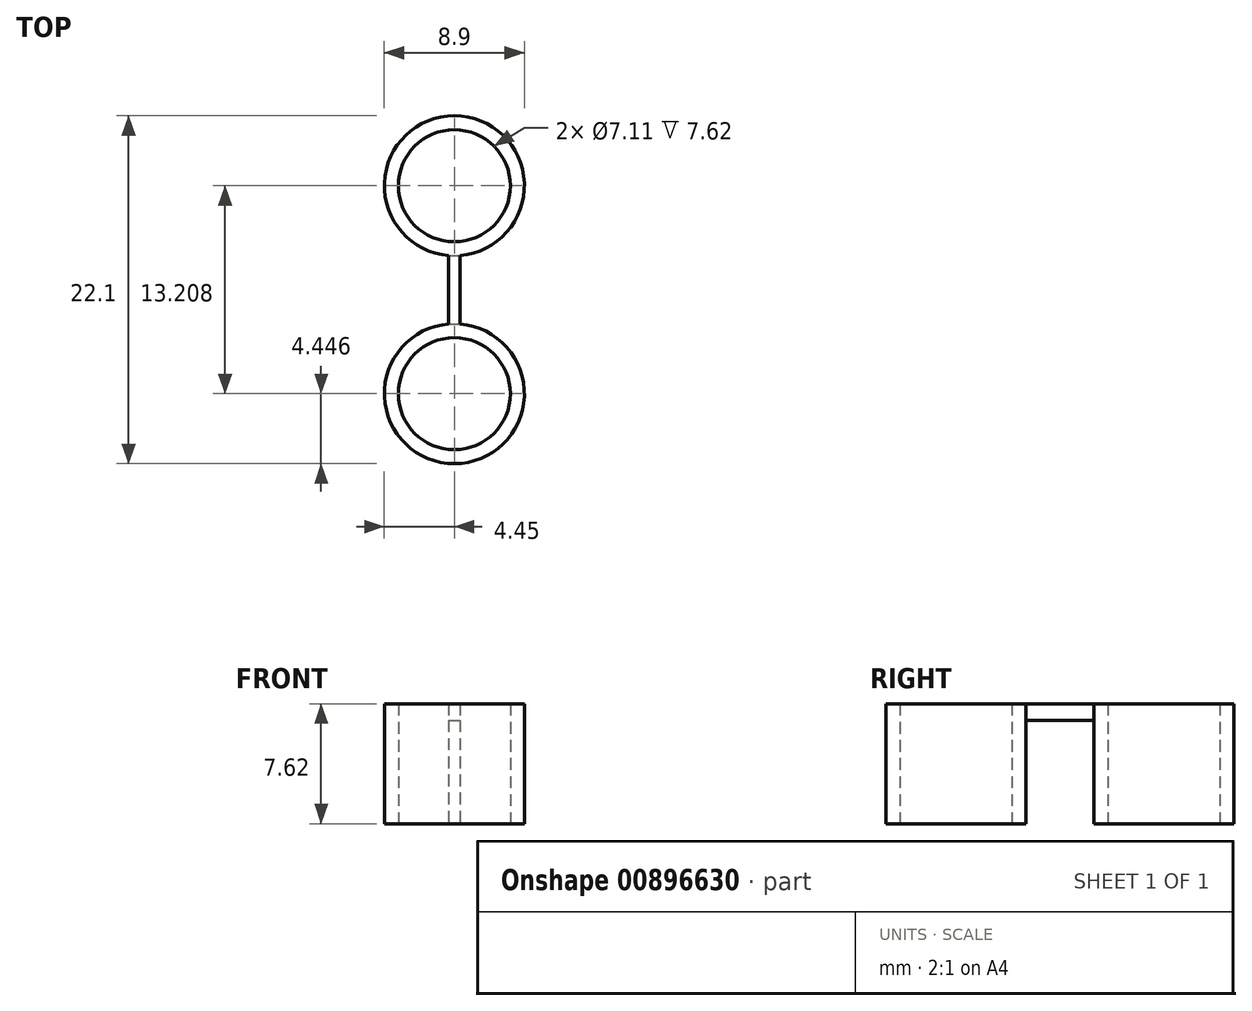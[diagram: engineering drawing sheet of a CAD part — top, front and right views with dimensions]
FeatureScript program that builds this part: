
annotation { "Feature Type Name" : "Feature", "Feature Type Description" : "" }
export const myFeature = defineFeature(function(context is Context, id is Id, definition is map)
    precondition{}
    {
        {
            var Q0;
            Q0=qCreatedBy(makeId("Top.planeOp"),FACE);
            var sketch = newSketch(context, id + "F0", { "sketchPlane" : qUnion([Q0])});
            skCircle(sketch, "E0", {"center": v(0, 6.6) * mm, "radius": 3.56 * mm});
            skCircle(sketch, "E1", {"center": v(0, -6.6) * mm, "radius": 3.56 * mm});
            skCircle(sketch, "E2", {"center": v(0, 6.6) * mm, "radius": 4.45 * mm});
            skCircle(sketch, "E3", {"center": v(0, -6.6) * mm, "radius": 4.45 * mm});
            skPoint(sketch, "E4.middle", {"position": v(0, 0) * mm});
            skLineSegment(sketch, "E5.bottom", {"start": v(0.36, -3.07) * mm, "end": v(-0.36, -3.07) * mm});
            skLineSegment(sketch, "E5.top", {"start": v(0.36, 3.07) * mm, "end": v(-0.36, 3.07) * mm});
            skLineSegment(sketch, "E5.left", {"start": v(0.36, -3.07) * mm, "end": v(0.36, 3.07) * mm});
            skLineSegment(sketch, "E5.right", {"start": v(-0.36, -3.07) * mm, "end": v(-0.36, 3.07) * mm});
            skSolve(sketch);
        }
        {
            var Q0;
            Q0 = qSketchRegion(id + "F0", true);
            extrude(context, id + "F1", {"entities" : qUnion([Q0]), "depth" : 7.62 * mm, "offsetDistance" : 25.4 * mm});
        }
        {
            var Q0;
            Q0=makeQuery(id+"F1.opExtrude","CAP_FACE",FACE,{"disambiguationData":[OSD([sQuery(id+"F0.wireOp",EDGE,"E0"),sQuery(id+"F0.wireOp",EDGE,"E1"),sQuery(id+"F0.wireOp",EDGE,"E2"),sQuery(id+"F0.wireOp",EDGE,"E3"),sQuery(id+"F0.wireOp",EDGE,"E5.left"),sQuery(id+"F0.wireOp",EDGE,"E5.right")])],"isStart":true});
            var sketch = newSketch(context, id + "F2", { "sketchPlane" : qUnion([Q0])});
            skLineSegment(sketch, "E6.bottom", {"start": v(-0.36, -2.17) * mm, "end": v(0.36, -2.17) * mm});
            skLineSegment(sketch, "E6.top", {"start": v(-0.36, 2.17) * mm, "end": v(0.36, 2.17) * mm});
            skLineSegment(sketch, "E6.left", {"start": v(-0.36, -2.17) * mm, "end": v(-0.36, 2.17) * mm});
            skLineSegment(sketch, "E6.right", {"start": v(0.36, -2.17) * mm, "end": v(0.36, 2.17) * mm});
            skPoint(sketch, "E6.middle", {"position": v(0, 0) * mm});
            skSolve(sketch);
        }
        {
            var Q0;
            Q0 = qSketchRegion(id + "F2", true);
            extrude(context, id + "F3", {"entities" : qUnion([Q0]), "operationType" : NewBodyOperationType.REMOVE, "oppositeDirection" : true, "depth" : 6.58 * mm, "offsetDistance" : 25.4 * mm});
        }
    });
